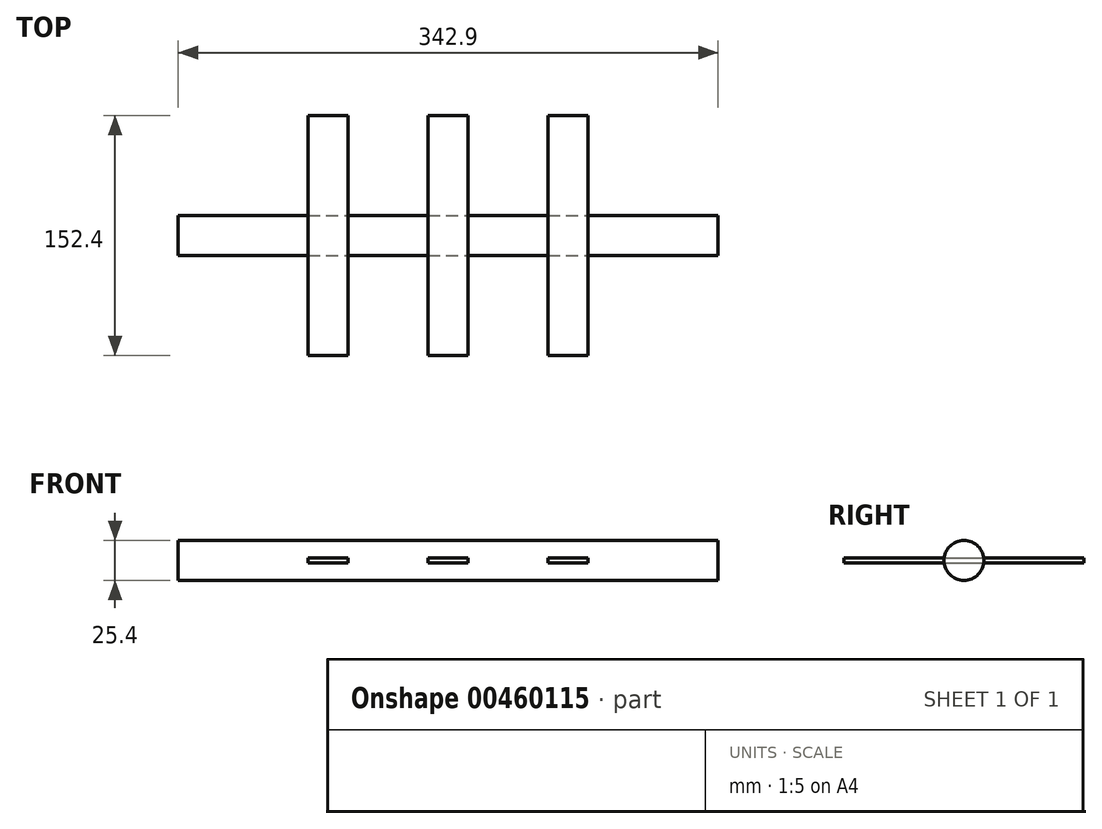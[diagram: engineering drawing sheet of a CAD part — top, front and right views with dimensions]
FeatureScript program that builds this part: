
annotation { "Feature Type Name" : "Feature", "Feature Type Description" : "" }
export const myFeature = defineFeature(function(context is Context, id is Id, definition is map)
    precondition{}
    {
        {
            var Q0;
            Q0=qCreatedBy(makeId("Front.planeOp"),FACE);
            var sketch = newSketch(context, id + "F0", { "sketchPlane" : qUnion([Q0])});
            skLineSegment(sketch, "E0.bottom", {"start": v(0, 0) * mm, "end": v(-342.9, 0) * mm});
            skLineSegment(sketch, "E0.top", {"start": v(0, 12.7) * mm, "end": v(-342.9, 12.7) * mm});
            skLineSegment(sketch, "E0.left", {"start": v(0, 0) * mm, "end": v(0, 12.7) * mm});
            skLineSegment(sketch, "E0.right", {"start": v(-342.9, 0) * mm, "end": v(-342.9, 12.7) * mm});
            skSolve(sketch);
        }
        {
            var Q0;
            Q0=makeQuery(id+"F0.imprint","IMPRINT",FACE,{"disambiguationData":[TD([[makeQuery(id+"F0.imprint","IMPRINT",EDGE,{"derivedFrom":sQuery(id+"F0.wireOp",EDGE,"E0.bottom")}),-1.0]])]});
            var sketch = newSketch(context, id + "F1", { "sketchPlane" : qUnion([Q0])});
            skLineSegment(sketch, "E1.bottom", {"start": v(-234.95, 1.59) * mm, "end": v(-260.35, 1.59) * mm});
            skLineSegment(sketch, "E1.top", {"start": v(-234.95, -1.59) * mm, "end": v(-260.35, -1.59) * mm});
            skLineSegment(sketch, "E1.left", {"start": v(-234.95, 1.59) * mm, "end": v(-234.95, -1.59) * mm});
            skLineSegment(sketch, "E1.right", {"start": v(-260.35, 1.59) * mm, "end": v(-260.35, -1.59) * mm});
            skPoint(sketch, "E1.middle", {"position": v(-247.65, 0) * mm});
            skSolve(sketch);
        }
        {
            var Q0;
            Q0=makeQuery(id+"F0.imprint","IMPRINT",FACE,{"disambiguationData":[TD([[makeQuery(id+"F0.imprint","IMPRINT",EDGE,{"derivedFrom":sQuery(id+"F0.wireOp",EDGE,"E0.bottom")}),-1.0]])]});
            var sketch = newSketch(context, id + "F2", { "sketchPlane" : qUnion([Q0])});
            skLineSegment(sketch, "E2.bottom", {"start": v(-158.75, 1.59) * mm, "end": v(-184.15, 1.59) * mm});
            skLineSegment(sketch, "E2.top", {"start": v(-158.75, -1.59) * mm, "end": v(-184.15, -1.59) * mm});
            skLineSegment(sketch, "E2.left", {"start": v(-158.75, 1.59) * mm, "end": v(-158.75, -1.59) * mm});
            skLineSegment(sketch, "E2.right", {"start": v(-184.15, 1.59) * mm, "end": v(-184.15, -1.59) * mm});
            skPoint(sketch, "E2.middle", {"position": v(-171.45, 0) * mm});
            skSolve(sketch);
        }
        {
            var Q0;
            Q0=makeQuery(id+"F0.imprint","IMPRINT",FACE,{"disambiguationData":[TD([[makeQuery(id+"F0.imprint","IMPRINT",EDGE,{"derivedFrom":sQuery(id+"F0.wireOp",EDGE,"E0.bottom")}),-1.0]])]});
            var sketch = newSketch(context, id + "F3", { "sketchPlane" : qUnion([Q0])});
            skLineSegment(sketch, "E3.bottom", {"start": v(-107.95, 1.59) * mm, "end": v(-82.55, 1.59) * mm});
            skLineSegment(sketch, "E3.top", {"start": v(-107.95, -1.59) * mm, "end": v(-82.55, -1.59) * mm});
            skLineSegment(sketch, "E3.left", {"start": v(-107.95, 1.59) * mm, "end": v(-107.95, -1.59) * mm});
            skLineSegment(sketch, "E3.right", {"start": v(-82.55, 1.59) * mm, "end": v(-82.55, -1.59) * mm});
            skPoint(sketch, "E3.middle", {"position": v(-95.25, 0) * mm});
            skSolve(sketch);
        }
        {
            var Q0;
            Q0 = qSketchRegion(id + "F1", true);
            var Q1;
            Q1 = qSketchRegion(id + "F2", true);
            var Q2;
            Q2 = qSketchRegion(id + "F3", true);
            extrude(context, id + "F4", {"entities" : qUnion([Q0, Q1, Q2]), "endBound" : BoundingType.SYMMETRIC, "depth" : 152.4 * mm, "offsetDistance" : 25.4 * mm});
        }
        {
            var Q0;
            Q0=makeQuery(id+"F0.imprint","IMPRINT",FACE,{"disambiguationData":[TD([[makeQuery(id+"F0.imprint","IMPRINT",EDGE,{"derivedFrom":sQuery(id+"F0.wireOp",EDGE,"E0.bottom")}),-1.0]])]});
            var Q1;
            Q1=sQuery(id+"F0.wireOp",EDGE,"E0.bottom");
            revolve(context, id + "F5", {"entities" : qUnion([Q0]), "axis" : qUnion([Q1]), "revolveType" : RevolveType.FULL});
        }
    });
